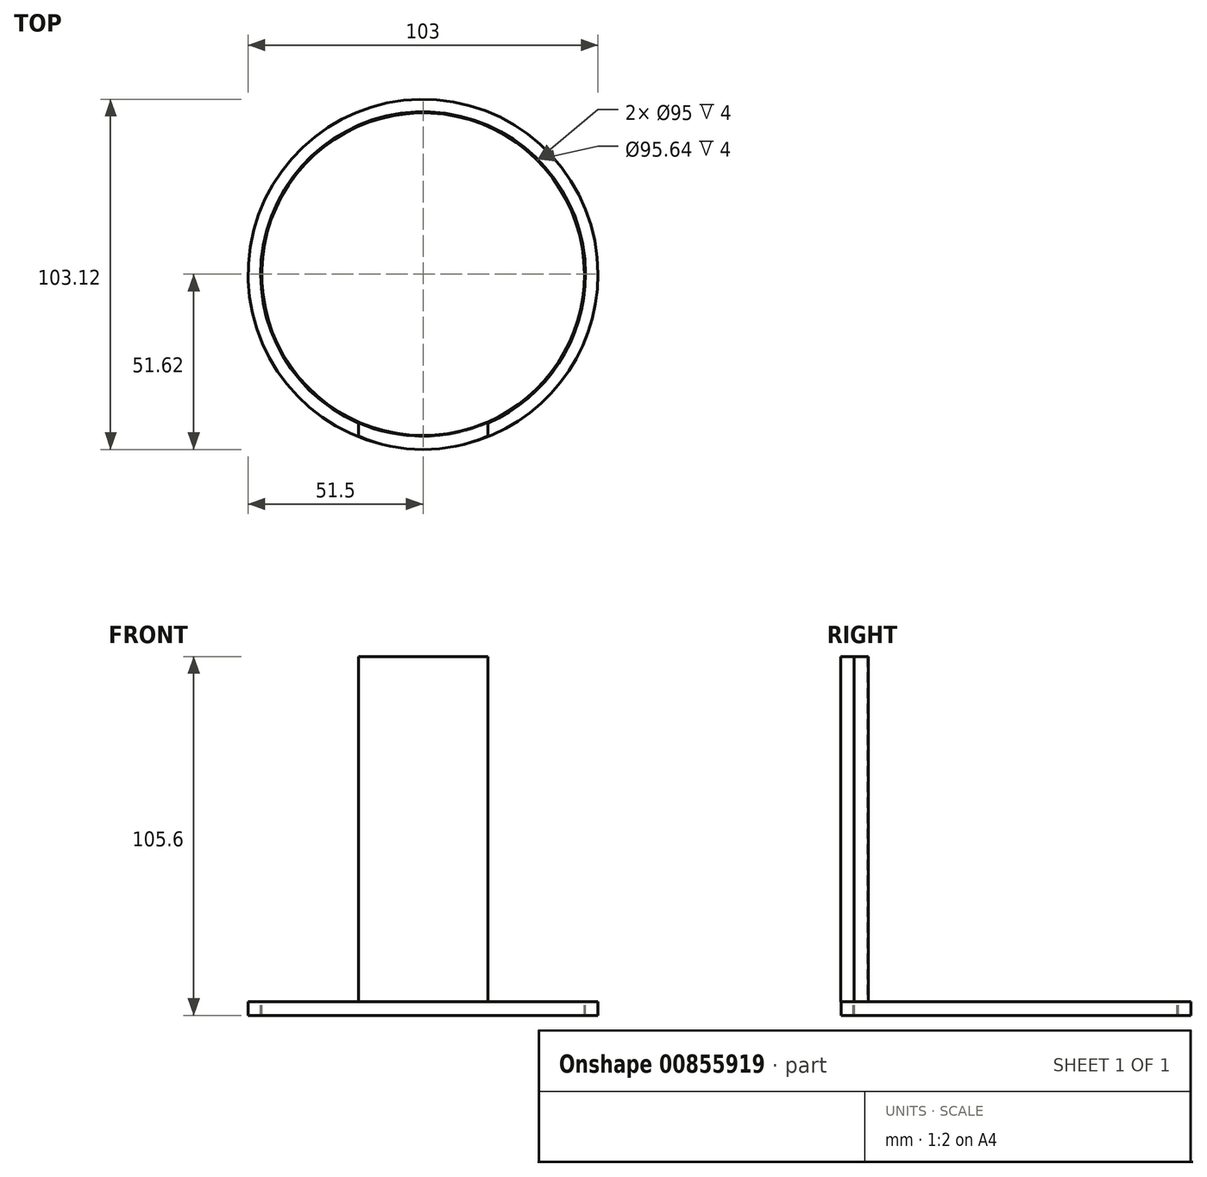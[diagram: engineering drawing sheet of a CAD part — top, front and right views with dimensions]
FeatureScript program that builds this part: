
annotation { "Feature Type Name" : "Feature", "Feature Type Description" : "" }
export const myFeature = defineFeature(function(context is Context, id is Id, definition is map)
    precondition{}
    {
        {
            var Q0;
            Q0=qCreatedBy(makeId("Top.planeOp"),FACE);
            var sketch = newSketch(context, id + "F0", { "sketchPlane" : qUnion([Q0])});
            skCircle(sketch, "E0", {"center": v(0, 0) * mm, "radius": 47.5 * mm});
            skCircle(sketch, "E1", {"center": v(0, 0) * mm, "radius": 51.5 * mm});
            skCircle(sketch, "E2", {"center": v(0, 0) * mm, "radius": 47.82 * mm});
            skCircle(sketch, "E3", {"center": v(0, 0) * mm, "radius": 20.23 * mm});
            skCircle(sketch, "E4", {"center": v(0, 0) * mm, "radius": 18.93 * mm});
            skSolve(sketch);
        }
        {
            var Q0;
            Q0=makeQuery(id+"F0.imprint","IMPRINT",FACE,{"disambiguationData":[TD([[makeQuery(id+"F0.imprint","IMPRINT",EDGE,{"derivedFrom":sQuery(id+"F0.wireOp",EDGE,"E0")}),-1.0]])]});
            extrude(context, id + "F1", {"entities" : qUnion([Q0]), "oppositeDirection" : true, "depth" : 4 * mm, "offsetDistance" : 25 * mm});
        }
        {
            var Q0;
            Q0=qSketchRegion(id+"F0",true);
            var Q1;
            Q1=makeQuery(id+"F1.opExtrude","CAP_FACE",FACE,{"disambiguationData":[OSD([sQuery(id+"F0.wireOp",EDGE,"E0"),sQuery(id+"F0.wireOp",EDGE,"E2")])],"isStart":true});
            extrude(context, id + "F2", {"entities" : qUnion([Q0, Q1]), "oppositeDirection" : true, "depth" : 4 * mm, "offsetDistance" : 25 * mm});
        }
        {
            var Q0;
            Q0=qCreatedBy(makeId("Top.planeOp"),FACE);
            var sketch = newSketch(context, id + "F3", { "sketchPlane" : qUnion([Q0])});
            skArc(sketch, "E5", {"start": v(-19.05, -47.64) * mm, "mid": v(0, -51.62) * mm, "end": v(19.05, -47.64) * mm});
            skArc(sketch, "E6", {"start": v(-19.05, -43.8) * mm, "mid": v(0.03, -47.64) * mm, "end": v(19.05, -43.5) * mm});
            skLineSegment(sketch, "E7", {"start": v(-19.05, -43.8) * mm, "end": v(-19.05, -47.64) * mm});
            skLineSegment(sketch, "E8", {"start": v(19.05, -43.5) * mm, "end": v(19.05, -47.64) * mm});
            skSolve(sketch);
        }
        {
            var Q0;
            Q0=qSketchRegion(id+"F3",true);
            extrude(context, id + "F4", {"entities" : qUnion([Q0]), "depth" : 101.6 * mm, "offsetDistance" : 25 * mm});
        }
    });
